# Revit family: Resideo_AxialTRV_V2000Ax
name_source: partatom
category: Pipe Fittings
units: mm (PartAtom-declared; Revit-internal decimal feet)

## family parameters
Always vertical = Yes
Cut with Voids When Loaded = No
OmniClass Number = 23.65.55.14
OmniClass Title = Valves for Liquid Services
Part Type = Elbow
Round Connector Dimension = Use Diameter
Shared = No
Work Plane-Based = No

## types (4) — shared parameters
Assembly Code = D2040100
AssetType = Fixed
BIMObjectName = Resideo_AxialTRV_V2000A
ClassificationName = Uniclass2015
ClassificationValue = Pr_65_54_95_89
DocumentationCertificates = https://www.bimstore.co
DocumentationInstallationGuide = https://www.bimstore.co
DocumentationLiterature = https://www.bimstore.co
DocumentationMaintenance = https://www.bimstore.co
DocumentationTechnical = https://www.bimstore.co
DurationUnit = Year
IfcExportAs = IfcValve
IfcExportType = IfcValveTypeEnum.REGULATING
Keynote = R11/180
Manufacturer = Resideo
ManufacturerName = Resideo
MaximumDifferentialPressure = 100000.0 Pa
MaximumDifferentialPressureForQuietOperation = 20000.0 Pa
MaximumMediumTemperature = 120 °С
MaximumOperatingPressure = 1000000.0 Pa
MediumType = Water or water-glycol mixture, quality to VDI 2035
MinimumMediumTemperature = -10 °С (without freezing)
NBSDescription = Thermostatic radiator valves
NBSObjectName = Resideo - Thermostatic radiator valves
NBSReference = 90-10-90/364
NominalLength = 30 mm  [stored 0.0984252 ft]
PresettableKV = Yes
PrimaryMaterial = Resideo - Stainless Steel - Brushed
ProductionYear = 2022
SecondaryMaterial = Resideo - Brass
ThermostatConnectionType = M30x1,5 (11,5 mm closing dimension)
URL = https://www.resideo.com
WarrantyDurationLabor = 0
WarrantyDurationParts = 0
WarrantyDurationUnit = Year
WarrantyGuarantorLabor = https://www.resideo.com
WarrantyGuarantorParts = https://www.resideo.com
_BSBibleVersion = 16
_CurrentRevision = 1
_DistributedBy = https://www.bimstore.co
_ObjectUserGuide = https://www.bimstore.co
pH-Value = 8 - 9.5
zero-valued in all types: Cost, ExpectedLife, _BimSpecGuid

## per-type parameters (varying)
| type | ConnectionDia | ConnectionSize | Connector1Offset | Connector2Offset | DNSize | Description | FlowCapacity | InsertType | ModelReference | NominalDepth | NominalHeight | Size | Type Comments | ValveInsertMaterial | ValveType |
| V2000ASX15 | 30 mm  [stored 0.0984252 ft] | 1/2 inch | 32 mm | 26 mm | 15 mm  [stored 0.0492126 ft] | TRV BODY, DN15 AXIAL, SX, RP1/2 | 0.2 L/s | VS1200SX01 (valve insert, SX-type) | TRV BODY, DN15 AXIAL, SX, RP1/2 | 48 mm | 100 mm  [stored 0.328084 ft] | DN15 | TRV BODY, DN15 AXIAL, SX, RP1/2 | Resideo - Plastic - Ivory | V2000, SX-type |
| V2000ASX10 | 20 mm  [stored 0.0656168 ft] | 3/8 inch | 31 mm | 22 mm  [stored 0.0721785 ft] | 10 mm  [stored 0.0328084 ft] | TRV BODY, DN10 AXIAL, SX, RP3/8 | 0.2 L/s | VS1200SX01 (valve insert, SX-type) | TRV BODY, DN10 AXIAL, SX, RP3/8 | 42 mm | 94 mm | DN10 | TRV BODY, DN10 AXIAL, SX, RP3/8 | Resideo - Plastic - Ivory | V2000, SX-type |
| V2000AFX10 | 20 mm  [stored 0.0656168 ft] | 3/8 inch | 31 mm | 22 mm  [stored 0.0721785 ft] | 10 mm  [stored 0.0328084 ft] | TRV BODY, DN10 AXIAL, FX, RP3/8 | 0.1 L/s | VS1200FX01 (valve insert, FX-type) | TRV BODY, DN10 AXIAL, FX, RP3/8 | 42 mm | 94 mm | DN10 | TRV BODY, DN10 AXIAL, FX, RP3/8 | Resideo - Plastic - Red | V2000, FX-type |
| V2000AFX15 | 30 mm  [stored 0.0984252 ft] | 1/2 inch | 32 mm | 26 mm | 15 mm  [stored 0.0492126 ft] | TRV BODY, DN15 AXIAL, FX, RP1/2 | 0.1 L/s | VS1200FX01 (valve insert, FX-type) | TRV BODY, DN15 AXIAL, FX, RP1/2 | 48 mm | 100 mm  [stored 0.328084 ft] | DN15 | TRV BODY, DN15 AXIAL, FX, RP1/2 | Resideo - Plastic - Red | V2000, FX-type |

note: column(s) folded — value = type name in every type: Model, ModelNumber, TypeName

type visibility flags (boolean, named after types; folded from table):
- V2000ASX15: Yes: V2000ASX15
- V2000ASX10: Yes: V2000ASX10
- V2000AFX10: Yes: V2000ASX10
- V2000AFX15: Yes: V2000ASX15

note: [stored X ft] marks values corroborated as IEEE doubles in the binary element streams (Revit-internal decimal feet)

## geometry (parser evidence)
native form markers: Sweep x2
no freeform markers — native parametric forms only
